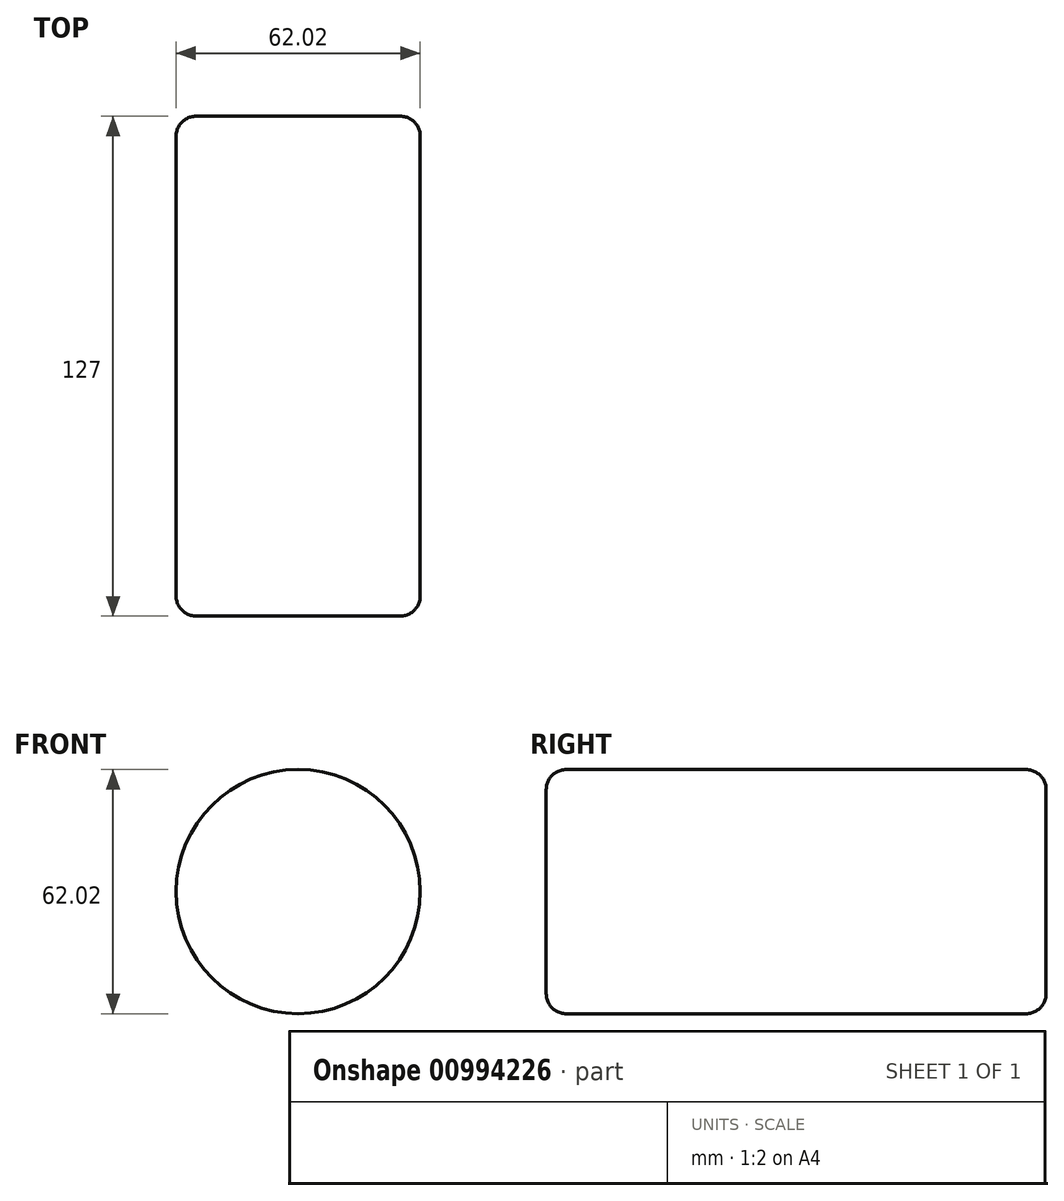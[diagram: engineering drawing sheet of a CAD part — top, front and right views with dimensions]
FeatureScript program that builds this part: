
annotation { "Feature Type Name" : "Feature", "Feature Type Description" : "" }
export const myFeature = defineFeature(function(context is Context, id is Id, definition is map)
    precondition{}
    {
        {
            var Q0;
            Q0=qCreatedBy(makeId("Front.planeOp"),FACE);
            var sketch = newSketch(context, id + "F0", { "sketchPlane" : qUnion([Q0])});
            skCircle(sketch, "E0", {"center": v(0, 0) * mm, "radius": 31.01 * mm});
            skLineSegment(sketch, "E1", {"start": v(31.01, 0) * mm, "end": v(78.58, 0) * mm});
            skLineSegment(sketch, "E2", {"start": v(0, 31.01) * mm, "end": v(0, 76.71) * mm});
            skLineSegment(sketch, "E3", {"start": v(-31.01, 0) * mm, "end": v(-77.09, 0) * mm});
            skLineSegment(sketch, "E4", {"start": v(0, -31.01) * mm, "end": v(0, -78.95) * mm});
            skSolve(sketch);
        }
        {
            var Q0;
            {var subQ0=sQuery(id+"F0.wireOp",EDGE,"E0");var subQ1=makeQuery(id+"F0.imprint","IMPRINT",VERTEX,{"disambiguationData":[OD(0.0)],"derivedFrom":subQ0});Q0=makeQuery(id+"F0.imprint","IMPRINT",FACE,{"disambiguationData":[TD([[makeQuery(id+"F0.imprint","IMPRINT",EDGE,{"disambiguationData":[TD([[subQ1,-1.0]])],"derivedFrom":subQ0}),1.0]])]});}
            extrude(context, id + "F1", {"entities" : qUnion([Q0]), "depth" : 127 * mm, "offsetDistance" : 25.4 * mm});
        }
        {
            var Q0;
            Q0=qCreatedBy(makeId("Front.planeOp"),FACE);
            var sketch = newSketch(context, id + "F2", { "sketchPlane" : qUnion([Q0])});
            skCircle(sketch, "E5", {"center": v(0, 0) * mm, "radius": 12.72 * mm});
            skSolve(sketch);
        }
        {
            var Q0;
            Q0=sQuery(id+"F2.wireOp",EDGE,"E5");
            extrude(context, id + "F3", {"bodyType" : ToolBodyType.SURFACE, "surfaceEntities" : qUnion([Q0]), "depth" : 254 * mm, "offsetDistance" : 25.4 * mm});
        }
        {
            var Q0;
            Q0=sQuery(id+"F0.wireOp",EDGE,"E2");
            var Q1;
            Q1=sQuery(id+"F0.wireOp",EDGE,"E1");
            var Q2;
            Q2=sQuery(id+"F0.wireOp",EDGE,"E3");
            var Q3;
            Q3=sQuery(id+"F0.wireOp",EDGE,"E4");
            extrude(context, id + "F4", {"bodyType" : ToolBodyType.SURFACE, "surfaceEntities" : qUnion([Q0, Q1, Q2, Q3]), "depth" : 76.2 * mm, "offsetDistance" : 25.4 * mm});
        }
        {
            var Q0;
            Q0=makeQuery(id+"F1.opExtrude","SWEPT_FACE",FACE,{"disambiguationData":[OSD([sQuery(id+"F0.wireOp",EDGE,"E0")])]});
            var Q1;
            Q1=makeQuery(id+"F1.opExtrude","CAP_FACE",FACE,{"disambiguationData":[OSD([sQuery(id+"F0.wireOp",EDGE,"E0")])],"isStart":false});
            fillet(context, id + "F5", {"entities" : qUnion([Q0, Q1]), "radius" : 5.08 * mm, "tangentPropagation" : true, "allowEdgeOverflow" : false});
        }
    });
